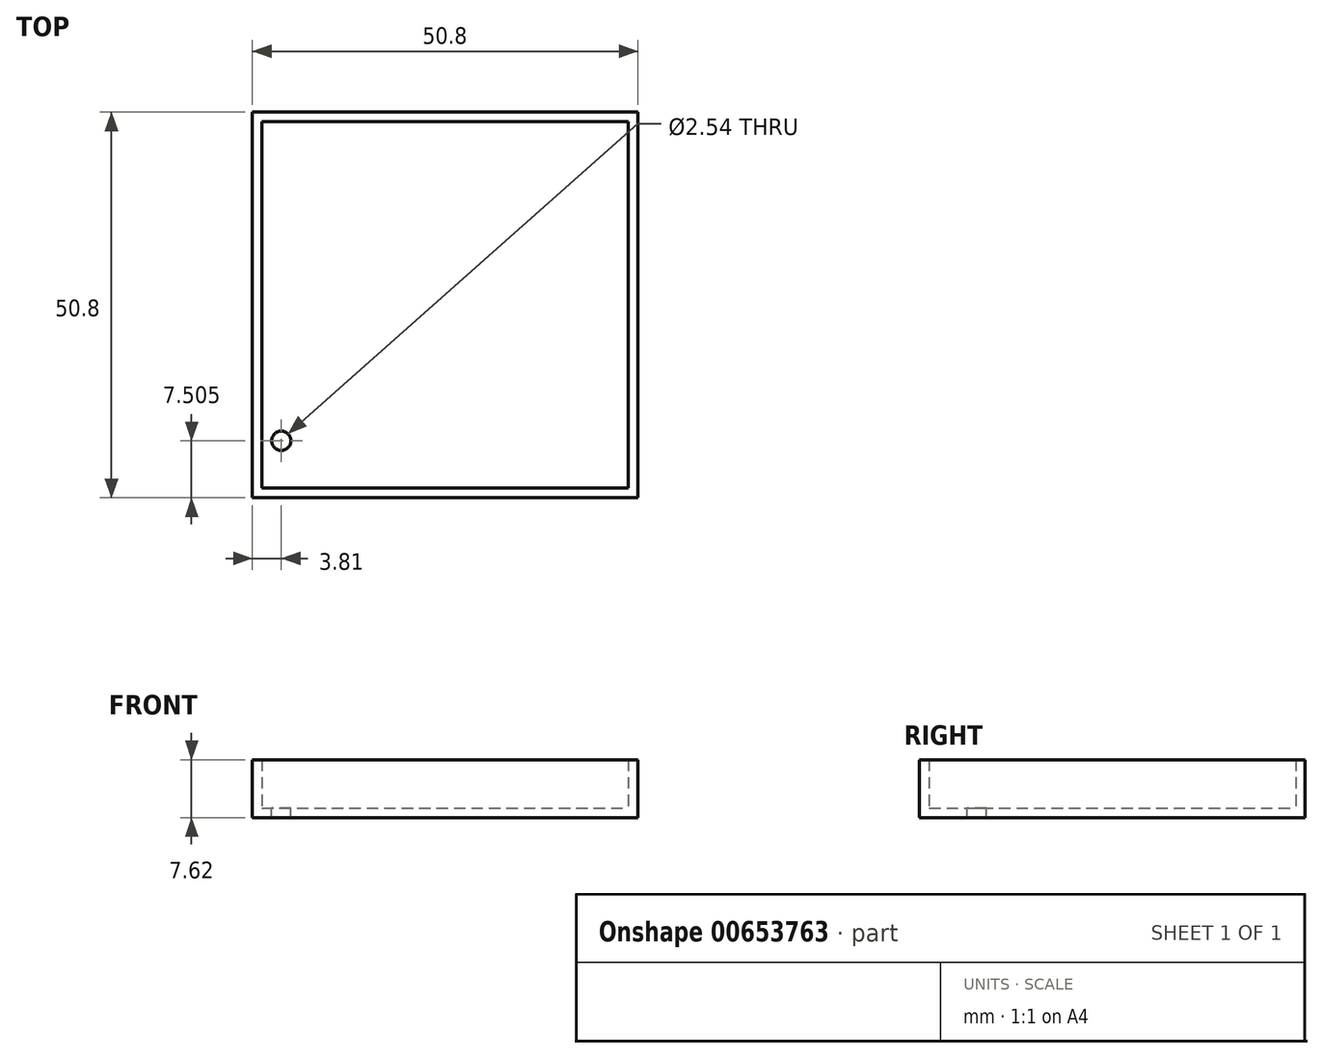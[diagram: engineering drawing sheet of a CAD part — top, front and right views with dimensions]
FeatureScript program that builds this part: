
annotation { "Feature Type Name" : "Feature", "Feature Type Description" : "" }
export const myFeature = defineFeature(function(context is Context, id is Id, definition is map)
    precondition{}
    {
        {
            var Q0;
            Q0=qCreatedBy(makeId("Top.planeOp"),FACE);
            var sketch = newSketch(context, id + "F0", { "sketchPlane" : qUnion([Q0])});
            skLineSegment(sketch, "E0.bottom", {"start": v(0, 0) * mm, "end": v(50.8, 0) * mm});
            skLineSegment(sketch, "E0.top", {"start": v(0, 50.8) * mm, "end": v(50.8, 50.8) * mm});
            skLineSegment(sketch, "E0.left", {"start": v(0, 0) * mm, "end": v(0, 50.8) * mm});
            skLineSegment(sketch, "E0.right", {"start": v(50.8, 0) * mm, "end": v(50.8, 50.8) * mm});
            skLineSegment(sketch, "E1", {"start": v(0, 0) * mm, "end": v(5.08, 0) * mm});
            skSolve(sketch);
        }
        {
            var Q0;
            Q0 = qSketchRegion(id + "F0", true);
            extrude(context, id + "F1", {"entities" : qUnion([Q0]), "depth" : 7.62 * mm, "offsetDistance" : 25.4 * mm});
        }
        {
            var Q0;
            Q0=makeQuery(id+"F1.opExtrude","CAP_FACE",FACE,{"disambiguationData":[OSD([sQuery(id+"F0.wireOp",EDGE,"E0.bottom"),sQuery(id+"F0.wireOp",EDGE,"E0.top"),sQuery(id+"F0.wireOp",EDGE,"E0.left"),sQuery(id+"F0.wireOp",EDGE,"E0.right")])],"isStart":false});
            shell(context, id + "F2", {"entities" : qUnion([Q0]), "thickness" : 1.27 * mm});
        }
        {
            var Q0;
            Q0=makeQuery(id+"F2.opShell","OFFSET_FACE",FACE,{"disambiguationData":[OSD([sQuery(id+"F0.wireOp",EDGE,"E0.bottom"),sQuery(id+"F0.wireOp",EDGE,"E0.top"),sQuery(id+"F0.wireOp",EDGE,"E0.left"),sQuery(id+"F0.wireOp",EDGE,"E0.right"),sQuery(id+"F0.wireOp",EDGE,"E1")])]});
            var sketch = newSketch(context, id + "F3", { "sketchPlane" : qUnion([Q0])});
            skLineSegment(sketch, "E2.bottom", {"start": v(6.35, 1.27) * mm, "end": v(7.62, 1.27) * mm});
            skLineSegment(sketch, "E2.top", {"start": v(6.35, 44.45) * mm, "end": v(7.62, 44.45) * mm});
            skLineSegment(sketch, "E2.left", {"start": v(6.35, 1.27) * mm, "end": v(6.35, 44.45) * mm});
            skLineSegment(sketch, "E2.right", {"start": v(7.62, 1.27) * mm, "end": v(7.62, 44.45) * mm});
            skLineSegment(sketch, "E3", {"start": v(6.35, 1.27) * mm, "end": v(1.27, 1.27) * mm});
            skCircle(sketch, "E4", {"center": v(3.81, 7.5) * mm, "radius": 1.27 * mm});
            skPoint(sketch, "E4.centerSnap0", {"position": v(3.81, 1.27) * mm});
            skSolve(sketch);
        }
        {
            var Q0;
            Q0=makeQuery(id+"F3.imprint","IMPRINT",FACE,{"disambiguationData":[TD([[makeQuery(id+"F3.imprint","IMPRINT",EDGE,{"derivedFrom":sQuery(id+"F3.wireOp",EDGE,"E4")}),1.0]])]});
            extrude(context, id + "F4", {"entities" : qUnion([Q0]), "operationType" : NewBodyOperationType.REMOVE, "oppositeDirection" : true, "depth" : 25.4 * mm, "offsetDistance" : 25.4 * mm});
        }
    });
